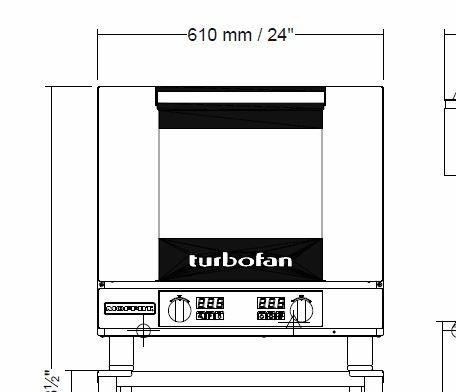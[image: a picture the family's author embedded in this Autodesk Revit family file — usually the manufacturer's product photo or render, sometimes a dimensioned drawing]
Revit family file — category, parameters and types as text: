
# Revit family: QF_MOFFAT_E30M3-2_NZ
name_source: partatom
category: Specialty Equipment
revit_build: Autodesk Revit 2014 (Build: 20130308_1515(x64)
units: mm (PartAtom-declared; Revit-internal decimal feet)

## types (1)
- QF_MOFFAT_E30M3-2_NZ
    Apparent Power = 2185 VA
    Conn Conduit = Yes
    Depth = 666 mm  [stored 2.18504 ft]
    Description = GN 1/1 MANUAL / ELECTRIC CONVECTION OVENS DOUBLE STACKED ON A STAINLESS STEEL BASE STAND
    Elec Conn Connection Height = 0 mm  [stored 0 ft]
    Elec Conn RI Height = 0 mm  [stored 0 ft]
    Electrical Remarks = 230-240V, 50Hz, 1P+N+E, 2.3kW, 9.5A
    Exhaust RI Height = 0 mm  [stored 0 ft]
    Exhaust Static Press = 0.00 in-wg
    Exhaust Vent Depth = 0 mm  [stored 0 ft]
    Exhaust Vent Diameter = 0 mm  [stored 0 ft]
    Exhaust Vent Width = 0 mm  [stored 0 ft]
    Exhaust Volume = 0 CFM
    FL Amps = 10 A
    Foodservice Equipment Identifier = Yes
    Height = 1636 mm  [stored 5.36745 ft]
    Height of Stand = 454 mm  [stored 1.4895 ft]
    Identify Quantity as Lot = Yes
    Length = 810 mm  [stored 2.65748 ft]
    Manufacturer = MOFFAT
    Max Overcurrent Protection = 0 A
    Min Ckt Ampacity = 0 A
    Model = E30M3-2
    Number of Poles = 1
    Phase = 1
    Volts = 230 V
    Watts = 2300 W
    Weight in Pounds = 0

note: [stored X ft] marks values corroborated as IEEE doubles in the binary element streams (Revit-internal decimal feet)

## geometry (parser evidence)
native form markers: Blend x14, Sweep x8
no freeform markers — native parametric forms only
